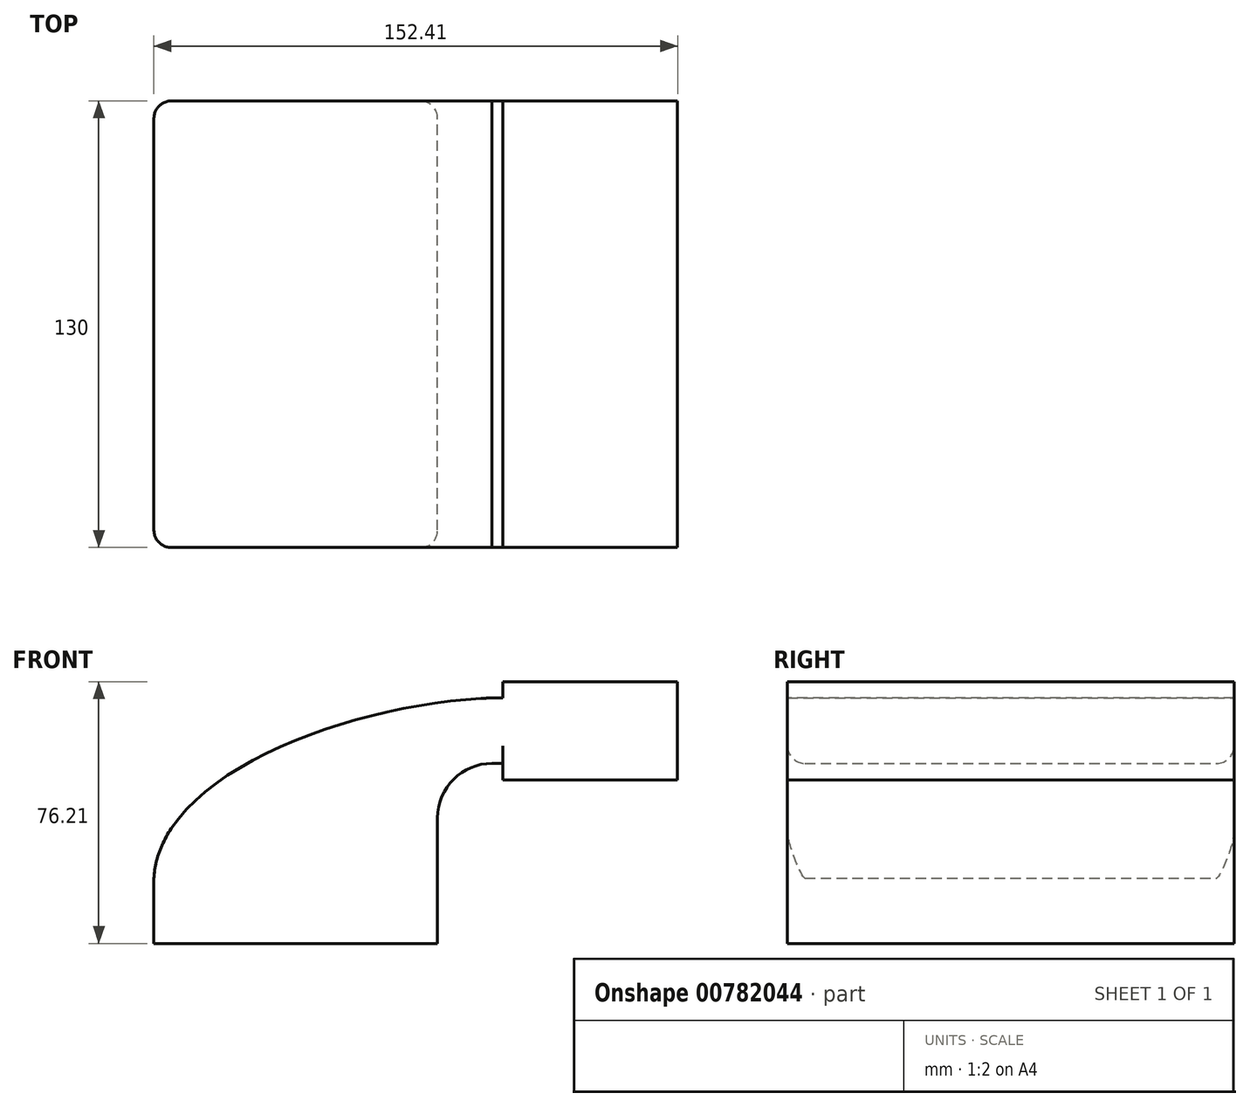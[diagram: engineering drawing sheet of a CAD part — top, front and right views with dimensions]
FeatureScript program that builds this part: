
annotation { "Feature Type Name" : "Feature", "Feature Type Description" : "" }
export const myFeature = defineFeature(function(context is Context, id is Id, definition is map)
    precondition{}
    {
        {
            var Q0;
            Q0=qCreatedBy(makeId("Front.planeOp"),FACE);
            var sketch = newSketch(context, id + "F0", { "sketchPlane" : qUnion([Q0])});
            skLineSegment(sketch, "E0.rect.bottom", {"start": v(-41.28, 9.52) * mm, "end": v(41.28, 9.52) * mm});
            skLineSegment(sketch, "E0.rect.top", {"start": v(-41.28, -9.52) * mm, "end": v(41.28, -9.52) * mm});
            skLineSegment(sketch, "E0.rect.left", {"start": v(-41.28, 9.52) * mm, "end": v(-41.28, -9.52) * mm});
            skLineSegment(sketch, "E0.rect.right", {"start": v(41.28, 9.52) * mm, "end": v(41.28, -9.52) * mm});
            skPoint(sketch, "E0.rect.middle", {"position": v(0, 0) * mm});
            skLineSegment(sketch, "E1", {"start": v(41.28, 9.52) * mm, "end": v(41.28, 27) * mm});
            skArc(sketch, "E2", {"start": v(41.28, 27) * mm, "mid": v(45.92, 38.23) * mm, "end": v(57.15, 42.88) * mm});
            skLineSegment(sketch, "E3", {"start": v(57.15, 42.88) * mm, "end": v(85.72, 42.88) * mm});
            skLineSegment(sketch, "E4.rect.bottom", {"start": v(60.32, 38.1) * mm, "end": v(111.12, 38.1) * mm});
            skLineSegment(sketch, "E4.rect.top", {"start": v(60.32, 66.68) * mm, "end": v(111.12, 66.68) * mm});
            skLineSegment(sketch, "E4.rect.left", {"start": v(60.32, 38.1) * mm, "end": v(60.32, 66.68) * mm});
            skLineSegment(sketch, "E4.rect.right", {"start": v(111.13, 38.1) * mm, "end": v(111.12, 66.68) * mm});
            skPoint(sketch, "E4.rect.middle", {"position": v(85.72, 52.39) * mm});
            skLineSegment(sketch, "E5.0", {"start": v(57.15, 61.93) * mm, "end": v(85.72, 61.93) * mm});
            skArc(sketch, "E5.1", {"start": v(22.23, 27) * mm, "mid": v(32.45, 51.7) * mm, "end": v(57.15, 61.93) * mm});
            skLineSegment(sketch, "E5.2", {"start": v(22.23, 9.52) * mm, "end": v(22.23, 27) * mm});
            skLineSegment(sketch, "E6", {"start": v(85.72, 38.1) * mm, "end": v(85.72, 66.68) * mm});
            skFitSpline(sketch, "E7", {"points": [v(-41.28, 9.53) * mm, v(57.15, 61.93) * mm], "startDerivative": vector(5.2, 92.34) * mm, "endDerivative": vector(120.92, 4.22) * mm});
            skSolve(sketch);
        }
        {
            var Q0;
            Q0=makeQuery(id+"F0.imprint","IMPRINT",FACE,{"disambiguationData":[TD([[makeQuery(id+"F0.imprint","IMPRINT",EDGE,{"derivedFrom":sQuery(id+"F0.wireOp",EDGE,"E0.rect.top")}),1.0]])]});
            var Q1;
            {var subQ3=sQuery(id+"F0.wireOp",EDGE,"E5.2");Q1=makeQuery(id+"F0.imprint","IMPRINT",FACE,{"disambiguationData":[TD([[makeQuery(id+"F0.imprint","IMPRINT",EDGE,{"derivedFrom":subQ3}),1.0]])]});}
            var Q2;
            {var subQ4=sQuery(id+"F0.wireOp",EDGE,"E1");Q2=makeQuery(id+"F0.imprint","IMPRINT",FACE,{"disambiguationData":[TD([[makeQuery(id+"F0.imprint","IMPRINT",EDGE,{"derivedFrom":subQ4}),1.0]])]});}
            var Q3;
            {var subQ0=sQuery(id+"F0.wireOp",EDGE,"E6");var subQ1=sQuery(id+"F0.wireOp",EDGE,"E3");var subQ2=makeQuery(id+"F0.imprint","INTERSECT",VERTEX,{"derivedFrom":[subQ1,subQ0]});Q3=makeQuery(id+"F0.imprint","IMPRINT",FACE,{"disambiguationData":[TD([[makeQuery(id+"F0.imprint","IMPRINT",EDGE,{"disambiguationData":[TD([[subQ2,1.0]])],"derivedFrom":subQ1}),1.0]])]});}
            var Q4;
            {var subQ0=sQuery(id+"F0.wireOp",EDGE,"E4.rect.left");var subQ1=sQuery(id+"F0.wireOp",EDGE,"E4.rect.top");var subQ2=makeQuery(id+"F0.imprint","INTERSECT",VERTEX,{"derivedFrom":[subQ1,subQ0]});Q4=makeQuery(id+"F0.imprint","IMPRINT",FACE,{"disambiguationData":[TD([[makeQuery(id+"F0.imprint","IMPRINT",EDGE,{"disambiguationData":[TD([[subQ2,-1.0]])],"derivedFrom":subQ1}),-1.0]])]});}
            var Q5;
            {var subQ0=sQuery(id+"F0.wireOp",EDGE,"E6");var subQ1=sQuery(id+"F0.wireOp",EDGE,"E3");var subQ2=makeQuery(id+"F0.imprint","INTERSECT",VERTEX,{"derivedFrom":[subQ1,subQ0]});Q5=makeQuery(id+"F0.imprint","IMPRINT",FACE,{"disambiguationData":[TD([[makeQuery(id+"F0.imprint","IMPRINT",EDGE,{"disambiguationData":[TD([[subQ2,1.0]])],"derivedFrom":subQ1}),-1.0]])]});}
            var Q6;
            {var subQ0=sQuery(id+"F0.wireOp",EDGE,"E4.rect.right");Q6=makeQuery(id+"F0.imprint","IMPRINT",FACE,{"disambiguationData":[TD([[makeQuery(id+"F0.imprint","IMPRINT",EDGE,{"derivedFrom":subQ0}),1.0]])]});}
            extrude(context, id + "F1", {"entities" : qUnion([Q0, Q1, Q2, Q3, Q4, Q5, Q6]), "endBound" : BoundingType.SYMMETRIC, "depth" : 130 * mm, "offsetDistance" : 25.4 * mm});
        }
        {
            var Q0;
            {var subQ9=sQuery(id+"F0.wireOp",EDGE,"E1");Q0=makeQuery(id+"F0.imprint","IMPRINT",FACE,{"disambiguationData":[TD([[makeQuery(id+"F0.imprint","IMPRINT",EDGE,{"derivedFrom":subQ9}),1.0]])]});}
            var Q1;
            {var subQ0=sQuery(id+"F0.wireOp",EDGE,"E6");var subQ1=sQuery(id+"F0.wireOp",EDGE,"E3");var subQ2=makeQuery(id+"F0.imprint","INTERSECT",VERTEX,{"derivedFrom":[subQ1,subQ0]});Q1=makeQuery(id+"F0.imprint","IMPRINT",FACE,{"disambiguationData":[TD([[makeQuery(id+"F0.imprint","IMPRINT",EDGE,{"disambiguationData":[TD([[subQ2,1.0]])],"derivedFrom":subQ1}),1.0]])]});}
            extrude(context, id + "F2", {"entities" : qUnion([Q0, Q1]), "operationType" : NewBodyOperationType.ADD, "endBound" : BoundingType.SYMMETRIC, "depth" : 50.8 * mm});
        }
        {
            var Q0;
            {var subQ3=sQuery(id+"F0.wireOp",EDGE,"E5.2");Q0=makeQuery(id+"F0.imprint","IMPRINT",FACE,{"disambiguationData":[TD([[makeQuery(id+"F0.imprint","IMPRINT",EDGE,{"derivedFrom":subQ3}),1.0]])]});}
            extrude(context, id + "F3", {"entities" : qUnion([Q0]), "operationType" : NewBodyOperationType.ADD, "endBound" : BoundingType.SYMMETRIC, "depth" : 15.88 * mm});
        }
        {
            var Q0;
            {var subQ5=sQuery(id+"F0.wireOp",EDGE,"E4.rect.right");Q0=makeQuery(id+"F0.imprint","IMPRINT",FACE,{"disambiguationData":[TD([[makeQuery(id+"F0.imprint","IMPRINT",EDGE,{"derivedFrom":subQ5}),1.0]])]});}
            var Q1;
            Q1=sQuery(id+"F0.wireOp",EDGE,"E6");
            revolve(context, id + "F4", {"operationType" : NewBodyOperationType.ADD, "entities" : qUnion([Q0]), "axis" : qUnion([Q1]), "revolveType" : RevolveType.FULL});
        }
        {
            var Q0;
            Q0=makeQuery(id+"F1.opExtrude","CAP_EDGE",EDGE,{"disambiguationData":[OSD([sQuery(id+"F0.wireOp",EDGE,"E0.rect.right")])],"isStart":false});
            var Q1;
            Q1=makeQuery(id+"F1.opExtrude","CAP_EDGE",EDGE,{"disambiguationData":[OSD([sQuery(id+"F0.wireOp",EDGE,"E0.rect.left")])],"isStart":false});
            var Q2;
            Q2=makeQuery(id+"F1.opExtrude","CAP_EDGE",EDGE,{"disambiguationData":[OSD([sQuery(id+"F0.wireOp",EDGE,"E0.rect.right")])],"isStart":true});
            var Q3;
            Q3=makeQuery(id+"F1.opExtrude","CAP_EDGE",EDGE,{"disambiguationData":[OSD([sQuery(id+"F0.wireOp",EDGE,"E0.rect.left")])],"isStart":true});
            fillet(context, id + "F5", {"entities" : qUnion([Q0, Q1, Q2, Q3]), "radius" : 5.08 * mm, "tangentPropagation" : true, "allowEdgeOverflow" : false});
        }
    });
